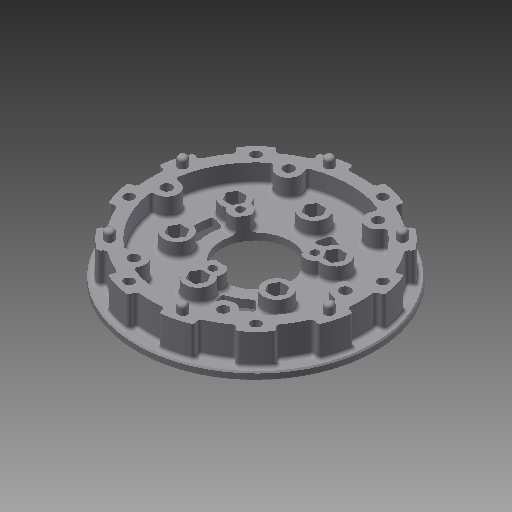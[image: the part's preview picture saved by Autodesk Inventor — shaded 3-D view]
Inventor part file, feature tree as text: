
AUTODESK INVENTOR PART (.ipt)
format: ipt  version: 2017 (Build 210142000, 142)  size: 2,313,216 bytes
history: native  units: in
note: dims shown in document units (in); Inventor stores cm internally (conversion verified against a paired STEP export)
features: fillet x1, other x1, imported_body x1
ambient origin geometry x8: Origin, YZ Plane, XZ Plane, XY Plane, X Axis, Y Axis, Z Axis, Center Point
bodies: Body1 (feature_tree)
feature tree (3):
  fillet  "Fillet18"  [1 undecoded]
  other  "217-2588-001 Rev4.ipt1"
  imported_body  "Base1"
note: 1 required parameter value undecoded (feature->parameter linkage not recoverable at this tier; creation-order binding heuristic only, values carry confidence <= 0.55)
